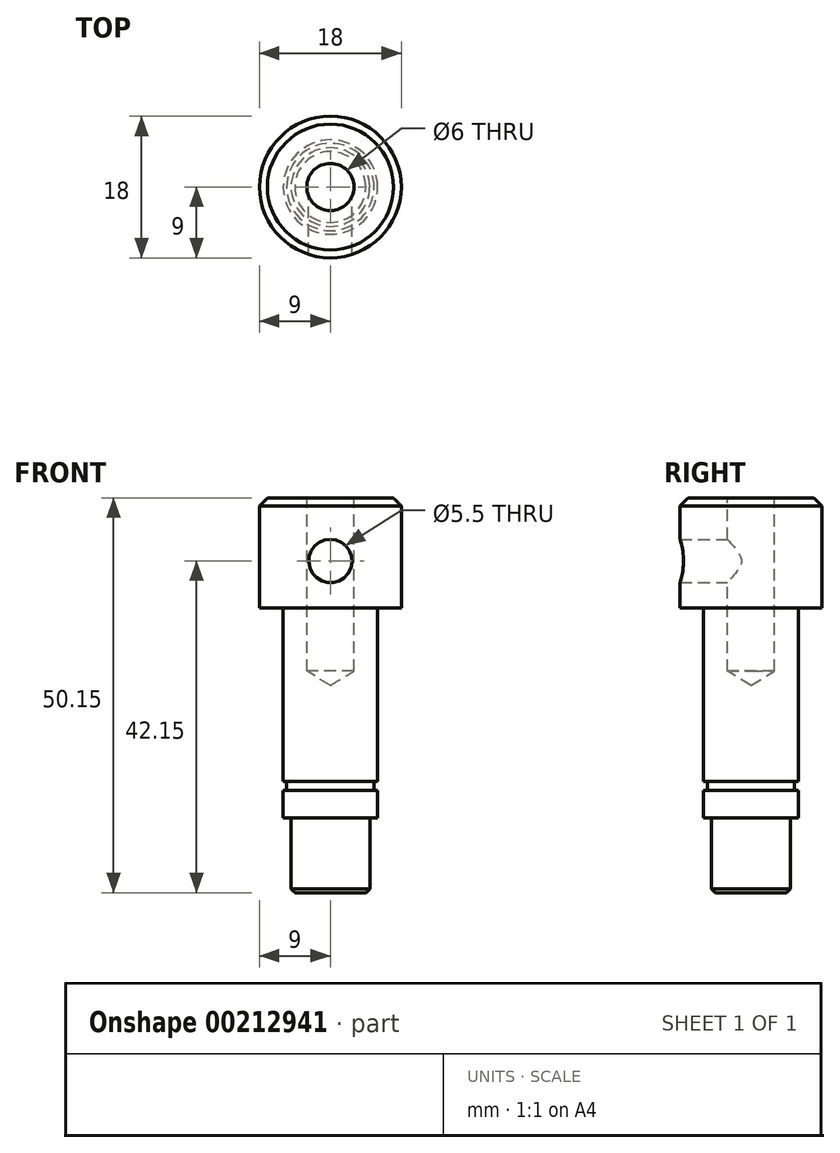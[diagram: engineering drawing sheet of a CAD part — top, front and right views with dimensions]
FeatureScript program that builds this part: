
annotation { "Feature Type Name" : "Feature", "Feature Type Description" : "" }
export const myFeature = defineFeature(function(context is Context, id is Id, definition is map)
    precondition{}
    {
        {
            var Q0;
            Q0=qCreatedBy(makeId("Top.planeOp"),FACE);
            var sketch = newSketch(context, id + "F0", { "sketchPlane" : qUnion([Q0])});
            skCircle(sketch, "E0", {"center": v(0, 0) * mm, "radius": 9 * mm});
            skSolve(sketch);
        }
        {
            var Q0;
            Q0 = qSketchRegion(id + "F0", true);
            extrude(context, id + "F1", {"entities" : qUnion([Q0]), "depth" : 14 * mm});
        }
        {
            var Q0;
            Q0=makeQuery(id+"F1.opExtrude","CAP_FACE",FACE,{"disambiguationData":[OSD([sQuery(id+"F0.wireOp",EDGE,"E0")])],"isStart":true});
            var sketch = newSketch(context, id + "F2", { "sketchPlane" : qUnion([Q0])});
            skCircle(sketch, "E1", {"center": v(0, 0) * mm, "radius": 6 * mm});
            skSolve(sketch);
        }
        {
            var Q0;
            Q0 = qSketchRegion(id + "F2", true);
            extrude(context, id + "F3", {"entities" : qUnion([Q0]), "operationType" : NewBodyOperationType.ADD, "depth" : 22 * mm});
        }
        {
            var Q0;
            Q0=makeQuery(id+"F3.opExtrude","CAP_FACE",FACE,{"disambiguationData":[OSD([sQuery(id+"F2.wireOp",EDGE,"E1")])],"isStart":false});
            var sketch = newSketch(context, id + "F4", { "sketchPlane" : qUnion([Q0])});
            skCircle(sketch, "E2", {"center": v(0, 0) * mm, "radius": 5.55 * mm});
            skSolve(sketch);
        }
        {
            var Q0;
            Q0 = qSketchRegion(id + "F4", true);
            extrude(context, id + "F5", {"entities" : qUnion([Q0]), "operationType" : NewBodyOperationType.ADD, "depth" : 1.15 * mm});
        }
        {
            var Q0;
            Q0=makeQuery(id+"F5.opExtrude","CAP_FACE",FACE,{"disambiguationData":[OSD([sQuery(id+"F4.wireOp",EDGE,"E2")])],"isStart":false});
            var sketch = newSketch(context, id + "F6", { "sketchPlane" : qUnion([Q0])});
            skCircle(sketch, "E3", {"center": v(0, 0) * mm, "radius": 6 * mm});
            skSolve(sketch);
        }
        {
            var Q0;
            Q0 = qSketchRegion(id + "F6", true);
            extrude(context, id + "F7", {"entities" : qUnion([Q0]), "operationType" : NewBodyOperationType.ADD, "depth" : 3.5 * mm});
        }
        {
            var Q0;
            Q0=makeQuery(id+"F7.opExtrude","CAP_FACE",FACE,{"disambiguationData":[OSD([sQuery(id+"F6.wireOp",EDGE,"E3")])],"isStart":false});
            var sketch = newSketch(context, id + "F8", { "sketchPlane" : qUnion([Q0])});
            skCircle(sketch, "E4", {"center": v(0, 0) * mm, "radius": 5 * mm});
            skSolve(sketch);
        }
        {
            var Q0;
            Q0 = qSketchRegion(id + "F8", true);
            extrude(context, id + "F9", {"entities" : qUnion([Q0]), "operationType" : NewBodyOperationType.ADD, "depth" : 9.5 * mm});
        }
        {
            var Q0;
            Q0=makeQuery(id+"F9.opExtrude","CAP_EDGE",EDGE,{"disambiguationData":[OSD([sQuery(id+"F8.wireOp",EDGE,"E4")])],"isStart":false});
            chamfer(context, id + "F10", {"entities" : qUnion([Q0]), "width" : .5 * mm, "tangentPropagation" : true});
        }
        {
            var Q0;
            Q0=makeQuery(id+"F1.opExtrude","CAP_EDGE",EDGE,{"disambiguationData":[OSD([sQuery(id+"F0.wireOp",EDGE,"E0")])],"isStart":false});
            chamfer(context, id + "F11", {"entities" : qUnion([Q0]), "width" : 1 * mm, "tangentPropagation" : true});
        }
        {
            var Q0;
            Q0=makeQuery(id+"F1.opExtrude","CAP_FACE",FACE,{"disambiguationData":[OSD([sQuery(id+"F0.wireOp",EDGE,"E0")])],"isStart":false});
            var sketch = newSketch(context, id + "F12", { "sketchPlane" : qUnion([Q0])});
            skPoint(sketch, "E5", {"position": v(0, 0) * mm});
            skSolve(sketch);
        }
        {
            var Q0;
            Q0=sQuery(id+"F12.wireOp",VERTEX,"E5");
            var Q1;
            Q1=makeQuery(id+"F1.opExtrude","SWEPT_BODY",BODY,{"disambiguationData":[OSD([sQuery(id+"F0.wireOp",EDGE,"E0")])]});
            hole(context, id + "F13", {"style" : HoleStyle.SIMPLE, "endStyle" : HoleEndStyle.BLIND, "holeDiameter" : 6 * mm, "holeDepth" : 22 * mm, "locations" : qUnion([Q0]), "scope" : qUnion([Q1])});
        }
        {
            var Q0;
            Q0=qCreatedBy(makeId("Front.planeOp"),FACE);
            var sketch = newSketch(context, id + "F14", { "sketchPlane" : qUnion([Q0])});
            skPoint(sketch, "E6", {"position": v(0, 6) * mm});
            skSolve(sketch);
        }
        {
            var Q0;
            Q0=sQuery(id+"F14.wireOp",VERTEX,"E6");
            var Q1;
            Q1=makeQuery(id+"F1.opExtrude","SWEPT_BODY",BODY,{"disambiguationData":[OSD([sQuery(id+"F0.wireOp",EDGE,"E0")])]});
            hole(context, id + "F15", {"style" : HoleStyle.SIMPLE, "endStyle" : HoleEndStyle.BLIND, "oppositeDirection" : true, "standardTappedOrClearance" : lookupTablePath({ "standard" : "ISO", "fit" : "Normal", "size" : "M5", "type" : "Clearance" }), "standardBlindInLast" : lookupTablePath({ "fit" : "Standard", "standard" : "ISO", "size" : "M5", "type" : "Clearance" }), "holeDiameter" : 5.5 * mm, "holeDepth" : 22 * mm, "locations" : qUnion([Q0]), "scope" : qUnion([Q1])});
        }
    });
